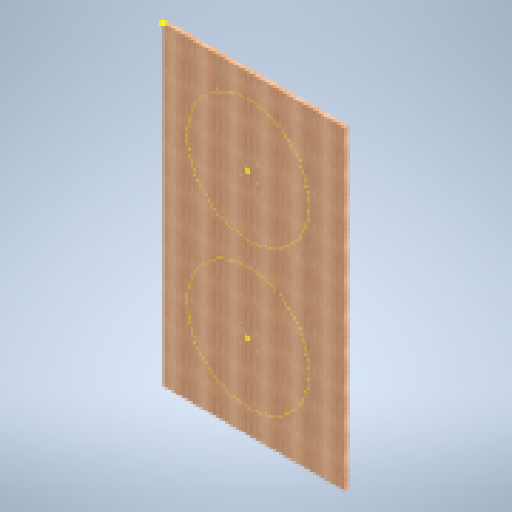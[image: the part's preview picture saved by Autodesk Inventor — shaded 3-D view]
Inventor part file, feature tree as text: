
AUTODESK INVENTOR PART (.ipt)
format: ipt  version: 2023 (Build 270158000, 158)  size: 409,088 bytes
history: native  units: mm
features: extrude x1, sketch x1
ambient origin geometry x8: Origin, YZ Plane, XZ Plane, XY Plane, X Axis, Y Axis, Z Axis, Center Point
bodies: Solid1 (feature_tree)
feature tree (2):
  extrude  "Extrusion1"  Depth=2600.0mm
  sketch  "Sketch2"  dims[d0=1500.0mm d1=2600.0mm d2=30.0mm d3=0.0mm d4=135.0mm d5=135.0mm d6=10.0mm d7=10.0mm d8=10.0mm d9=10.0mm d10=1010.0mm d13=45.0deg d14=650.0mm d15=1010.0mm d16=650.0mm d17=750.0mm d18=750.0mm]
